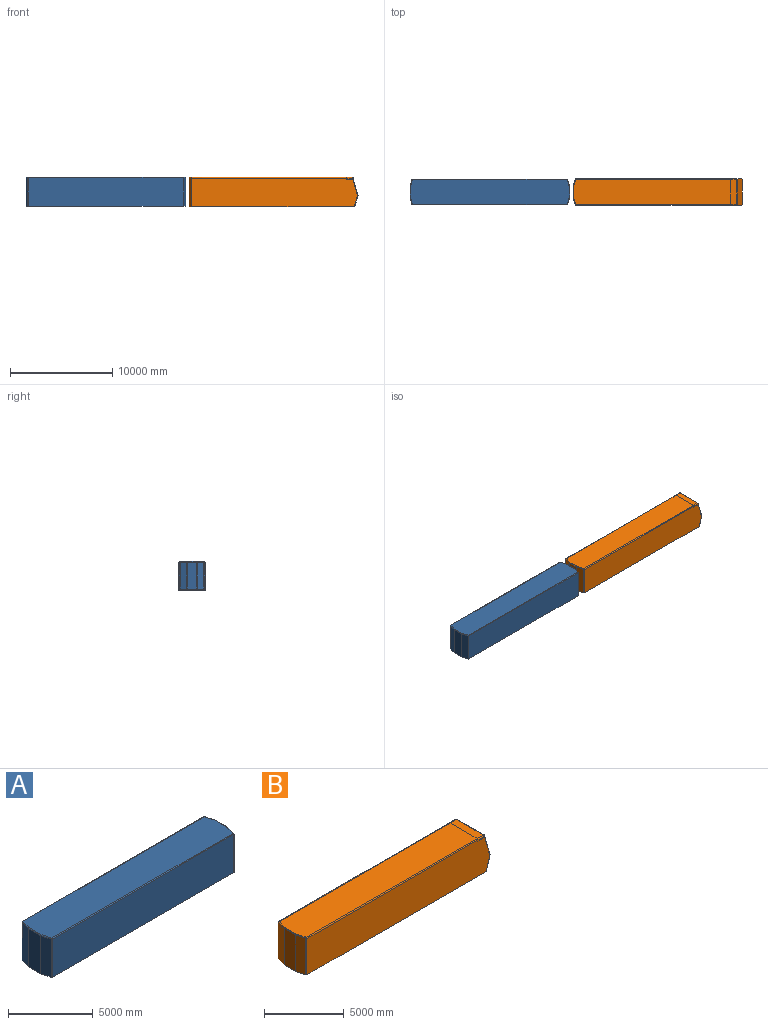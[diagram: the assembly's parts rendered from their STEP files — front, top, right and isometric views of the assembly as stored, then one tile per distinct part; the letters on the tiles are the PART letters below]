
ASSEMBLY  parts=2 mates=1
PART A: 36 faces, bbox 15580x2500x2800 mm
  f0: sphere r=50.8mm, area 3381.1mm2, adj f1,f2,f15
  f1: cylinder r=50.8mm len=2749.2mm, axis (0,0,1), area 182980.8mm2, adj f0,f19,f21,f25
  f2: cylinder r=50.8mm len=15101.94mm, axis (-1,0,0), area 1205081.5mm2, adj f0,f3,f23,f25
  f3: sphere r=50.8mm, area 3381.1mm2, adj f2,f4,f5
  f4: cylinder r=50.8mm len=2749.2mm, axis (0,0,-1), area 182980.8mm2, adj f3,f18,f21,f25
  f5: cylinder r=50.8mm len=725.38mm, axis (0.26,0.97,0), area 58631.3mm2, adj f3,f9,f18,f23
  f6: sphere r=50.8mm, area 3381.1mm2, adj f7,f8,f10
  f7: cylinder r=50.8mm len=2749.2mm, axis (0,0,1), area 182980.8mm2, adj f6,f16,f21,f22
  f8: cylinder r=50.8mm len=725.38mm, axis (-0.26,0.97,0), area 58631.3mm2, adj f6,f9,f16,f23
  f9: cylinder r=50.8mm len=1000mm, axis (0,1,0), area 79410.4mm2, adj f5,f8,f17,f23
  f10: cylinder r=50.8mm len=15101.94mm, axis (1,0,0), area 1205081.5mm2, adj f6,f11,f22,f23
  f11: sphere r=50.8mm, area 3381.1mm2, adj f10,f12,f13
  f12: cylinder r=50.8mm len=2749.2mm, axis (0,0,-1), area 182980.8mm2, adj f11,f20,f21,f22
  f13: cylinder r=50.8mm len=725.38mm, axis (-0.26,-0.97,0), area 58631.3mm2, adj f11,f14,f20,f23
  f14: cylinder r=50.8mm len=1000mm, axis (0,-1,0), area 79410.4mm2, adj f13,f15,f23,f24
  f15: cylinder r=50.8mm len=725.38mm, axis (0.26,-0.97,0), area 58631.3mm2, adj f0,f14,f19,f23
  f16: plane 2749.2x712.29mm, normal (-0.97,-0.26,0), area 2026655.8mm2, adj f7,f8,f17,f21
  f17: plane 2749.2x1000mm, normal (-1,0,0), area 2749200mm2, adj f9,f16,f18,f21
  f18: plane 2749.2x712.29mm, normal (-0.97,0.26,0), area 2026655.8mm2, adj f4,f5,f17,f21
  f19: plane 2749.2x712.29mm, normal (0.97,0.26,0), area 2026655.8mm2, adj f1,f15,f21,f24
  f20: plane 2749.2x712.29mm, normal (0.97,-0.26,0), area 2026655.8mm2, adj f12,f13,f21,f24
  f21: plane 15580x2500mm, normal (0,0,-1), area 38648831.7mm2, adj f1,f4,f7,f12,f16,f17,f18,f19
  f22: plane 15101.94x2749.2mm, normal (0,-1,0), area 41518261.5mm2, adj f7,f10,f12,f21
  f23: plane 15478.4x2398.4mm, normal (0,0,1), area 36857669.7mm2, adj f2,f5,f8,f9,f10,f13,f14,f15
  f24: plane 2749.2x1000mm, normal (1,0,0), area 2749200mm2, adj f14,f19,f20,f21
  f25: plane 15101.94x2749.2mm, normal (0,1,0), area 41518261.5mm2, adj f1,f2,f4,f21
  f26: plane 2596.8x973.37mm, normal (-1,0,0), area 2527652.2mm2, adj f27,f30,f31,f32
  f27: plane 15376.8x2296.8mm, normal (0,0,-1), area 35083906mm2, adj f26,f28,f29,f31,f32,f33,f34,f35
  f28: plane 15023.89x2596.8mm, normal (0,-1,0), area 39014026.8mm2, adj f27,f30,f32,f33
  f29: plane 15023.89x2596.8mm, normal (0,1,0), area 39014026.8mm2, adj f27,f30,f31,f35
  f30: plane 15376.8x2296.8mm, normal (0,0,1), area 35083906mm2, adj f26,f28,f29,f31,f32,f33,f34,f35
  f31: plane 2596.8x661.71mm, normal (-0.97,0.26,0), area 1778386.3mm2, adj f26,f27,f29,f30
  f32: plane 2596.8x661.71mm, normal (-0.97,-0.26,0), area 1778386.3mm2, adj f26,f27,f28,f30
  f33: plane 2596.8x661.71mm, normal (0.97,-0.26,0), area 1778386.3mm2, adj f27,f28,f30,f34
  f34: plane 2596.8x973.37mm, normal (1,0,0), area 2527652.2mm2, adj f27,f30,f33,f35
  f35: plane 2596.8x661.71mm, normal (0.97,0.26,0), area 1778386.3mm2, adj f27,f29,f30,f34
PART B: 38 faces, bbox 16478x2540x2865.2 mm
  f0: plane 599.25x99.2mm, normal (0,-1,0), area 58067.5mm2, adj f1,f18,f30
  f1: cylinder r=76.2mm len=571.47mm, axis (1,0,0), area 67187.2mm2, adj f0,f2,f13,f17,f31
  f2: bspline ~73.38x73.38mm, area 4374.8mm2, adj f1,f3,f31
  f3: cylinder r=76.2mm len=2436.52mm, axis (0,-1,0), area 238940.4mm2, adj f2,f5,f17,f19
  f4: bspline ~51.74x50.84mm, area 1215.5mm2, adj f5,f6,f19,f20
  f5: plane 2438.4x1705.68mm, normal (0.96,0,0.27), area 4319078.8mm2, adj f3,f4,f20,f21,f26,f29,f30,f31
  f6: cylinder r=76.2mm len=571.47mm, axis (-1,0,0), area 67187.2mm2, adj f4,f7,f9,f17,f19
  f7: plane 599.25x99.2mm, normal (0,1,0), area 58067.5mm2, adj f6,f8,f20
  f8: plane 16184.22x2774.6mm, normal (0,1,0), area 44271789.1mm2, adj f7,f9,f12,f21,f22,f37
  f9: cylinder r=76.2mm len=15143.85mm, axis (1,0,0), area 1812122.3mm2, adj f6,f8,f10,f11
  f10: bspline ~76.2x76.2mm, area 6281.8mm2, adj f9,f15,f36,f37
  f11: plane 15329.2x2387.6mm, normal (0,0,1), area 36469152.8mm2, adj f9,f13,f17,f34,f35,f36
  f12: plane 16124.58x2540.05mm, normal (0,0,-1), area 40797590.3mm2, adj f8,f14,f15,f16,f18,f22,f25,f27
  f13: cylinder r=76.2mm len=15140.97mm, axis (-1,0,0), area 1811777.6mm2, adj f1,f11,f18,f33
  f14: plane 2800x1000mm, normal (-1,0,0), area 2800000mm2, adj f12,f15,f16,f35
  f15: plane 2800x726.89mm, normal (-0.97,0.26,0), area 2106270.1mm2, adj f10,f12,f14,f36,f37
  f16: plane 2800x737.69mm, normal (-0.97,-0.26,0), area 2137566.2mm2, adj f12,f14,f32,f33,f34
  f17: plane 2387.6x545.09mm, normal (0,0,1), area 1301464.9mm2, adj f1,f3,f6,f11
  f18: plane 16181.34x2774.6mm, normal (0,-1,0), area 44263798.4mm2, adj f0,f12,f13,f27,f29,f32
  f19: bspline ~73.38x73.38mm, area 4375.1mm2, adj f3,f4,f6
  f20: cylinder r=50.8mm len=112.9mm, axis (-0.27,0,0.96), area 8220.2mm2, adj f4,f5,f7,f21
  f21: cylinder r=50.8mm len=1613.33mm, axis (0.27,0,-0.96), area 132553.9mm2, adj f5,f8,f20,f24
  f22: cylinder r=50.8mm len=1090.16mm, axis (-0.28,0,-0.96), area 87870.7mm2, adj f8,f12,f23,f24,f25
  f23: plane 2438.4x1024.97mm, normal (0.96,0,-0.28), area 2605942.2mm2, adj f22,f25,f26,f27
  f24: sphere r=50.8mm, area 1445.4mm2, adj f21,f22,f26
  f25: cylinder r=50.8mm len=2535.84mm, axis (0,1,0), area 162714.4mm2, adj f12,f22,f23,f27
  f26: cylinder r=50.8mm len=2438.4mm, axis (0,-1,0), area 69378.9mm2, adj f5,f23,f24,f28
  f27: cylinder r=50.8mm len=1090.16mm, axis (0.28,0,0.96), area 87870.7mm2, adj f12,f18,f23,f25,f28
  f28: sphere r=50.8mm, area 1445.4mm2, adj f26,f27,f29
  f29: cylinder r=50.8mm len=1613.33mm, axis (-0.27,0,0.96), area 132553.9mm2, adj f5,f18,f28,f30
  f30: cylinder r=50.8mm len=112.9mm, axis (0.27,0,-0.96), area 8220.2mm2, adj f0,f5,f29,f31
  f31: bspline ~51.74x50.84mm, area 1215.5mm2, adj f1,f2,f5,f30
  f32: cylinder r=50.8mm len=2774.6mm, axis (0,0,1), area 184671.4mm2, adj f12,f16,f18,f33
  f33: bspline ~76.2x76.2mm, area 6281.8mm2, adj f13,f16,f32,f34
  f34: cylinder r=50.8mm len=725.38mm, axis (-0.26,0.97,0), area 58631.3mm2, adj f11,f16,f33,f35
  f35: cylinder r=50.8mm len=1000mm, axis (0,1,0), area 79410.4mm2, adj f11,f14,f34,f36
  f36: cylinder r=50.8mm len=714.58mm, axis (0.26,0.97,0), area 57739.4mm2, adj f10,f11,f15,f35
  f37: cylinder r=50.8mm len=2774.6mm, axis (0,0,-1), area 184671.4mm2, adj f8,f10,f12,f15
PLACE A t=(-15875,0,0)mm
PLACE B t=(47.32,5.35,-25.4)mm
MATE planar B.f11 <-> A.f23  axis (0,0,1) through (7790,1250,2800)mm
